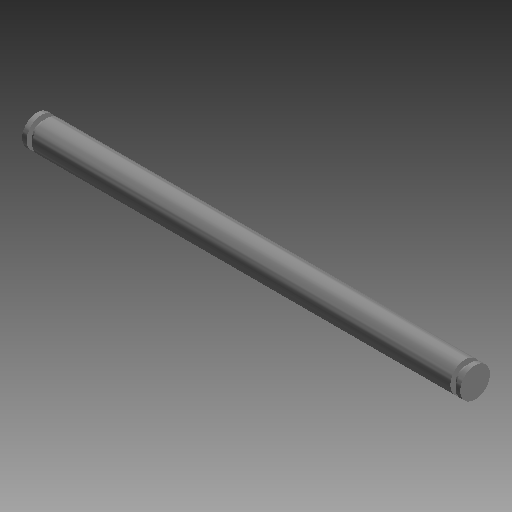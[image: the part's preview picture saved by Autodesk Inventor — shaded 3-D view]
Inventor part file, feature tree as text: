
AUTODESK INVENTOR PART (.ipt)
format: ipt  version: 2019 (Build 230136000, 136)  size: 73,216 bytes
history: native  units: mm (DEFAULTED — no unit token found)
features: revolve x1
ambient origin geometry x8: Origin, YZ Plane, XZ Plane, XY Plane, X Axis, Y Axis, Z Axis, Center Point
bodies: Solid1 (feature_tree)
feature tree (1):
  revolve  "Revolve1"  [1 undecoded]
note: 1 required parameter value undecoded (feature->parameter linkage not recoverable at this tier; creation-order binding heuristic only, values carry confidence <= 0.55)
